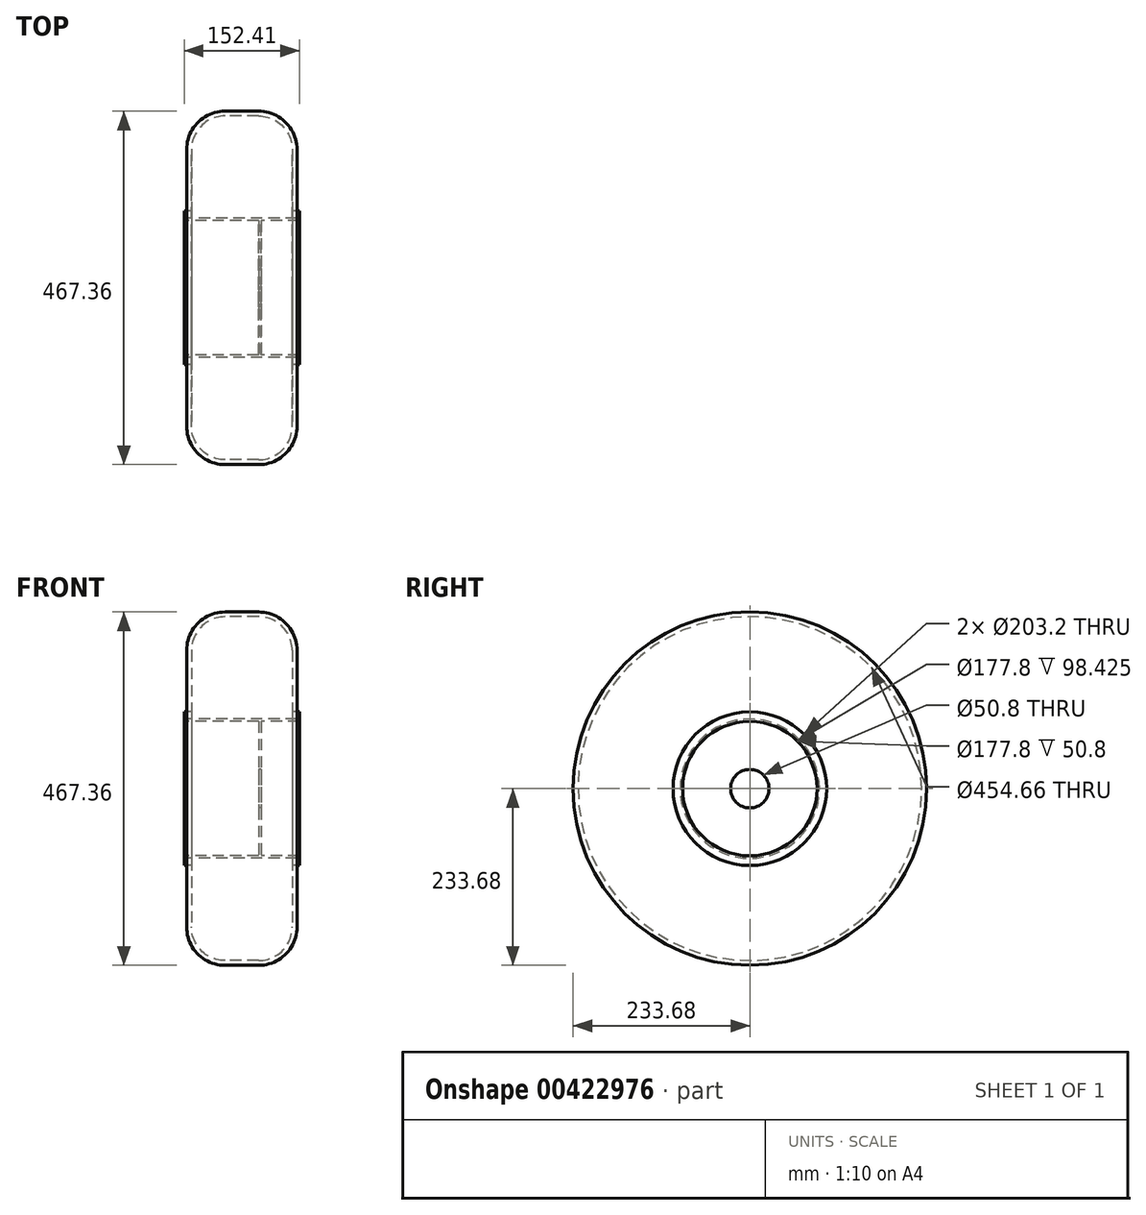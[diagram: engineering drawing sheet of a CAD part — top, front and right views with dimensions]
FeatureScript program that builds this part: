
annotation { "Feature Type Name" : "Feature", "Feature Type Description" : "" }
export const myFeature = defineFeature(function(context is Context, id is Id, definition is map)
    precondition{}
    {
        {
            var Q0;
            Q0=qCreatedBy(makeId("Front.planeOp"),FACE);
            var sketch = newSketch(context, id + "F0", { "sketchPlane" : qUnion([Q0])});
            skLineSegment(sketch, "E0", {"start": v(0, 25.4) * mm, "end": v(0, 88.9) * mm});
            skLineSegment(sketch, "E1", {"start": v(0, 88.9) * mm, "end": v(-98.43, 88.9) * mm});
            skLineSegment(sketch, "E2", {"start": v(-98.43, 88.9) * mm, "end": v(-98.43, 101.6) * mm});
            skLineSegment(sketch, "E3", {"start": v(-98.43, 101.6) * mm, "end": v(-95.25, 101.6) * mm});
            skLineSegment(sketch, "E4", {"start": v(53.97, 101.6) * mm, "end": v(53.97, 88.9) * mm});
            skLineSegment(sketch, "E5", {"start": v(53.97, 88.9) * mm, "end": v(3.17, 88.9) * mm});
            skLineSegment(sketch, "E6", {"start": v(3.17, 88.9) * mm, "end": v(3.17, 25.4) * mm});
            skLineSegment(sketch, "E7", {"start": v(-95.25, 101.6) * mm, "end": v(-95.25, 92.07) * mm});
            skLineSegment(sketch, "E8", {"start": v(-95.25, 92.07) * mm, "end": v(50.8, 92.08) * mm});
            skLineSegment(sketch, "E9", {"start": v(50.8, 92.08) * mm, "end": v(50.8, 101.6) * mm});
            skLineSegment(sketch, "E10.trimOffspring", {"start": v(50.8, 101.6) * mm, "end": v(53.97, 101.6) * mm});
            skLineSegment(sketch, "E11", {"start": v(-95.25, 101.6) * mm, "end": v(-95.25, 182.88) * mm});
            skLineSegment(sketch, "E12", {"start": v(50.8, 101.6) * mm, "end": v(50.8, 182.88) * mm});
            skLineSegment(sketch, "E13", {"start": v(0, 233.68) * mm, "end": v(-44.45, 233.68) * mm});
            skLineSegment(sketch, "E14", {"start": v(-95.25, 101.6) * mm, "end": v(-88.9, 101.6) * mm});
            skLineSegment(sketch, "E15", {"start": v(44.45, 101.6) * mm, "end": v(50.8, 101.6) * mm});
            skPoint(sketch, "E16.visualSharp", {"position": v(-95.25, 233.68) * mm});
            skArc(sketch, "E16.filletArc", {"start": v(-44.45, 233.68) * mm, "mid": v(-80.37, 218.8) * mm, "end": v(-95.25, 182.88) * mm});
            skPoint(sketch, "E17.visualSharp", {"position": v(50.8, 233.68) * mm});
            skArc(sketch, "E17.filletArc", {"start": v(50.8, 182.88) * mm, "mid": v(35.92, 218.8) * mm, "end": v(0, 233.68) * mm});
            skPoint(sketch, "E18.visualSharp", {"position": v(-66.68, 227.33) * mm});
            skLineSegment(sketch, "E19.0", {"start": v(44.45, 101.6) * mm, "end": v(44.45, 182.88) * mm});
            skLineSegment(sketch, "E19.1", {"start": v(-88.9, 101.6) * mm, "end": v(-88.9, 182.88) * mm});
            skArc(sketch, "E19.2", {"start": v(-44.45, 227.33) * mm, "mid": v(-75.88, 214.31) * mm, "end": v(-88.9, 182.88) * mm});
            skLineSegment(sketch, "E19.3", {"start": v(0, 227.33) * mm, "end": v(-44.45, 227.33) * mm});
            skArc(sketch, "E19.4", {"start": v(44.45, 182.88) * mm, "mid": v(31.43, 214.31) * mm, "end": v(0, 227.33) * mm});
            skLineSegment(sketch, "E20", {"start": v(0, 0) * mm, "end": v(3.18, 0) * mm, "construction": true});
            skLineSegment(sketch, "E21", {"start": v(3.18, 25.4) * mm, "end": v(0, 25.4) * mm});
            skSolve(sketch);
        }
        {
            var Q0;
            Q0=makeQuery(id+"F0.imprint","IMPRINT",FACE,{"disambiguationData":[TD([[makeQuery(id+"F0.imprint","IMPRINT",EDGE,{"derivedFrom":sQuery(id+"F0.wireOp",EDGE,"E11")}),-1.0]])]});
            var Q1;
            Q1=makeQuery(id+"F0.imprint","IMPRINT",FACE,{"disambiguationData":[TD([[makeQuery(id+"F0.imprint","IMPRINT",EDGE,{"derivedFrom":sQuery(id+"F0.wireOp",EDGE,"E0")}),-1.0]])]});
            var Q2;
            Q2=sQuery(id+"F0.wireOp",EDGE,"E20");
            revolve(context, id + "F1", {"entities" : qUnion([Q0, Q1]), "axis" : qUnion([Q2]), "revolveType" : RevolveType.FULL});
        }
    });
